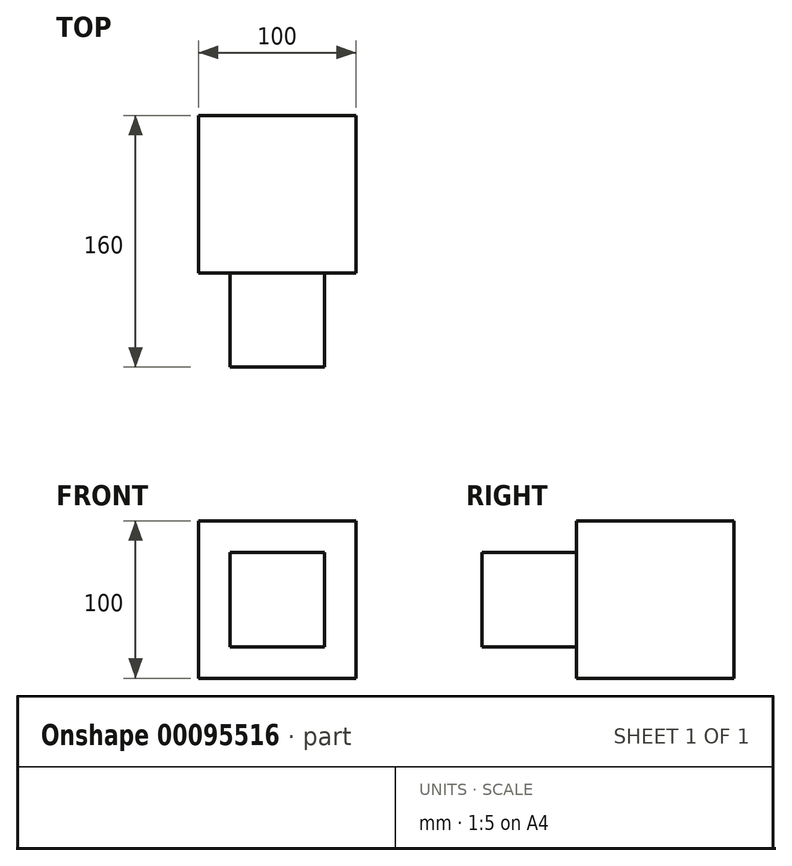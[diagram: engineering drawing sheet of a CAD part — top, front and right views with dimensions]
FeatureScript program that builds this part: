
annotation { "Feature Type Name" : "Feature", "Feature Type Description" : "" }
export const myFeature = defineFeature(function(context is Context, id is Id, definition is map)
    precondition{}
    {
        {
            var Q0;
            Q0=qCreatedBy(makeId("Front.planeOp"),FACE);
            var sketch = newSketch(context, id + "F0", { "sketchPlane" : qUnion([Q0])});
            skLineSegment(sketch, "E0.bottom", {"start": v(-49, 52.76) * mm, "end": v(51, 52.76) * mm});
            skLineSegment(sketch, "E0.top", {"start": v(-49, -47.24) * mm, "end": v(51, -47.24) * mm});
            skLineSegment(sketch, "E0.left", {"start": v(-49, 52.76) * mm, "end": v(-49, -47.24) * mm});
            skLineSegment(sketch, "E0.right", {"start": v(51, 52.76) * mm, "end": v(51, -47.24) * mm});
            skSolve(sketch);
        }
        {
            var Q0;
            Q0 = qSketchRegion(id + "F0", true);
            extrude(context, id + "F1", {"entities" : qUnion([Q0]), "depth" : 100 * mm});
        }
        {
            var Q0;
            Q0=makeQuery(id+"F1.opExtrude","CAP_FACE",FACE,{"disambiguationData":[OSD([sQuery(id+"F0.wireOp",EDGE,"E0.bottom"),sQuery(id+"F0.wireOp",EDGE,"E0.top"),sQuery(id+"F0.wireOp",EDGE,"E0.left"),sQuery(id+"F0.wireOp",EDGE,"E0.right")])],"isStart":false});
            var sketch = newSketch(context, id + "F2", { "sketchPlane" : qUnion([Q0])});
            skLineSegment(sketch, "E1.bottom", {"start": v(31.02, 32.76) * mm, "end": v(-28.98, 32.76) * mm});
            skLineSegment(sketch, "E1.top", {"start": v(31.02, -27.24) * mm, "end": v(-28.98, -27.24) * mm});
            skLineSegment(sketch, "E1.left", {"start": v(31.02, 32.76) * mm, "end": v(31.02, -27.24) * mm});
            skLineSegment(sketch, "E1.right", {"start": v(-28.98, 32.76) * mm, "end": v(-28.98, -27.24) * mm});
            skSolve(sketch);
        }
        {
            var Q0;
            Q0=makeQuery(id+"F2.imprint","IMPRINT",FACE,{"disambiguationData":[TD([[makeQuery(id+"F2.imprint","IMPRINT",EDGE,{"derivedFrom":sQuery(id+"F2.wireOp",EDGE,"E1.bottom")}),1.0]])]});
            extrude(context, id + "F3", {"entities" : qUnion([Q0]), "operationType" : NewBodyOperationType.ADD, "depth" : 60 * mm});
        }
    });
